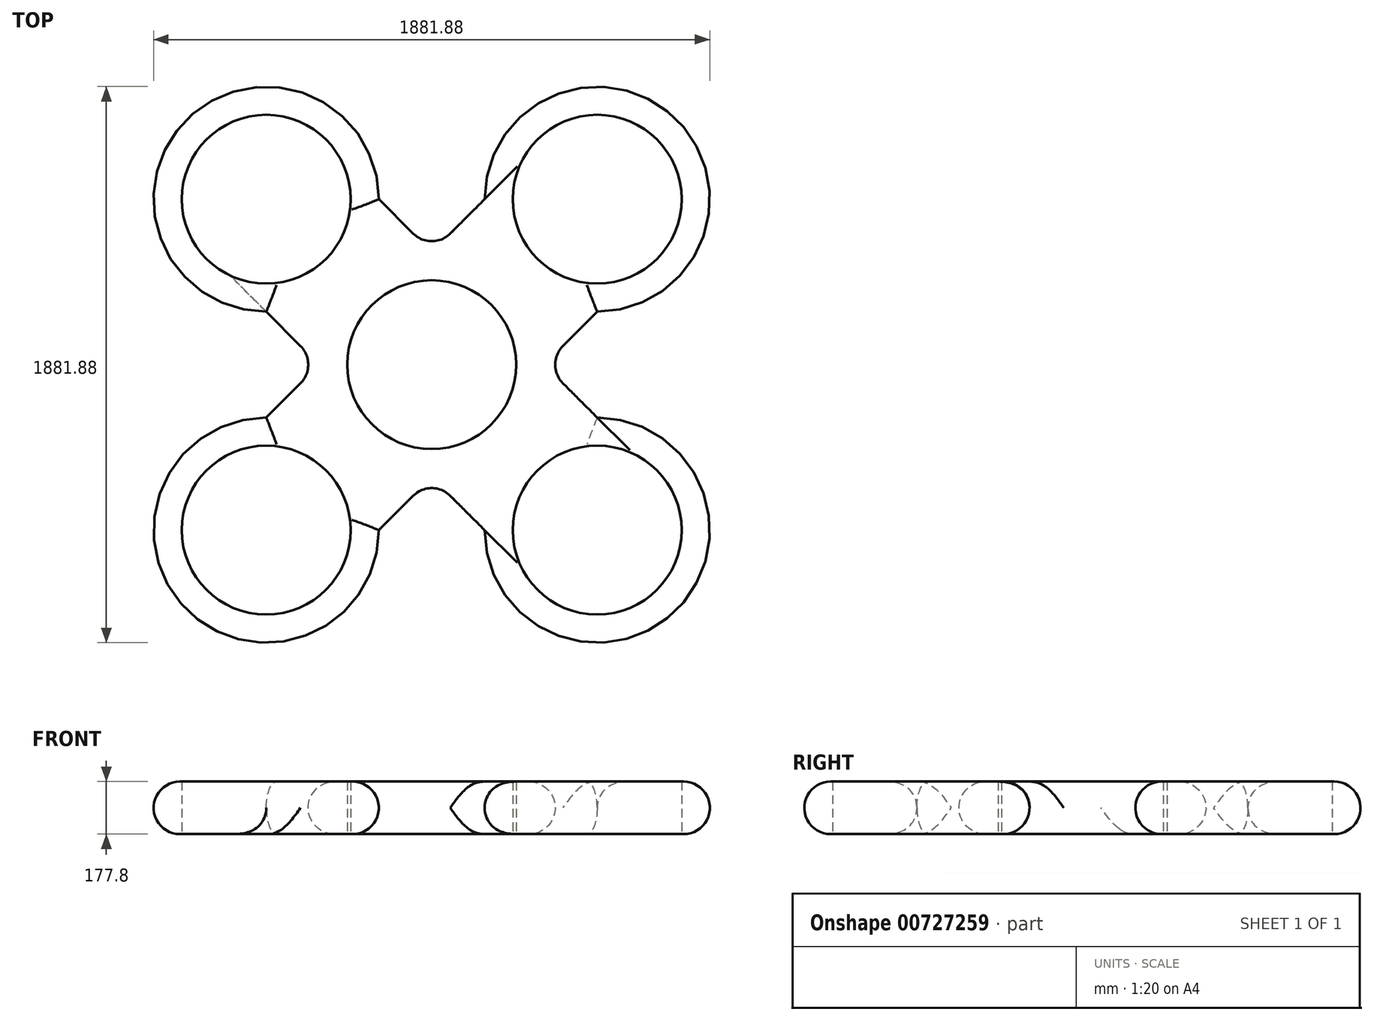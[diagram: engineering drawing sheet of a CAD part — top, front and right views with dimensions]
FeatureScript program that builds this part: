
annotation { "Feature Type Name" : "Feature", "Feature Type Description" : "" }
export const myFeature = defineFeature(function(context is Context, id is Id, definition is map)
    precondition{}
    {
        {
            var Q0;
            Q0=qCreatedBy(makeId("Top.planeOp"),FACE);
            var sketch = newSketch(context, id + "F0", { "sketchPlane" : qUnion([Q0])});
            skCircle(sketch, "E0", {"center": v(0, 0) * mm, "radius": 285.75 * mm});
            skCircle(sketch, "E1", {"center": v(0, 0) * mm, "radius": 381 * mm});
            skLineSegment(sketch, "E2", {"start": v(0, 0) * mm, "end": v(0, 762) * mm});
            skPoint(sketch, "E3.0.midPoint", {"position": v(0, 762) * mm});
            skCircle(sketch, "E4", {"center": v(-559.94, 559.94) * mm, "radius": 285.75 * mm});
            skCircle(sketch, "E5", {"center": v(-559.94, 559.94) * mm, "radius": 381 * mm});
            skLineSegment(sketch, "E6", {"start": v(0, 381) * mm, "end": v(-178.94, 559.94) * mm});
            skLineSegment(sketch, "E7", {"start": v(-381, 0) * mm, "end": v(-559.94, 178.94) * mm});
            skCircle(sketch, "E8", {"center": v(559.94, 559.94) * mm, "radius": 285.75 * mm});
            skCircle(sketch, "E9", {"center": v(559.94, 559.94) * mm, "radius": 381 * mm});
            skLineSegment(sketch, "E10", {"start": v(0, 381) * mm, "end": v(178.94, 559.94) * mm});
            skLineSegment(sketch, "E11", {"start": v(381, 0) * mm, "end": v(559.94, 178.94) * mm});
            skCircle(sketch, "E12", {"center": v(559.94, -559.94) * mm, "radius": 285.75 * mm});
            skCircle(sketch, "E13", {"center": v(559.94, -559.94) * mm, "radius": 381 * mm});
            skLineSegment(sketch, "E14", {"start": v(0, -381) * mm, "end": v(178.94, -559.94) * mm});
            skLineSegment(sketch, "E15", {"start": v(381, 0) * mm, "end": v(559.94, -178.94) * mm});
            skCircle(sketch, "E16", {"center": v(-559.94, -559.94) * mm, "radius": 285.75 * mm});
            skCircle(sketch, "E17", {"center": v(-559.94, -559.94) * mm, "radius": 381 * mm});
            skLineSegment(sketch, "E18", {"start": v(-381, 0) * mm, "end": v(-559.94, -178.94) * mm});
            skLineSegment(sketch, "E19", {"start": v(0, -381) * mm, "end": v(-178.94, -559.94) * mm});
            skSolve(sketch);
        }
        {
            var Q0;
            {var subQ0=sQuery(id+"F0.wireOp",EDGE,"sOMEycEi-MdqB-uUI0-WZba-tYQb8DUVvBA8");Q0=makeQuery(id+"F0.imprint","IMPRINT",FACE,{"disambiguationData":[TD([[makeQuery(id+"F0.imprint","IMPRINT",EDGE,{"derivedFrom":subQ0}),1.0]])]});}
            var Q1;
            {var subQ0=sQuery(id+"F0.wireOp",EDGE,"q6DWFzyf-PYHz-5VbU-MnMN-QwQLJZp00MLm");Q1=makeQuery(id+"F0.imprint","IMPRINT",FACE,{"disambiguationData":[TD([[makeQuery(id+"F0.imprint","IMPRINT",EDGE,{"derivedFrom":subQ0}),1.0]])]});}
            var Q2;
            {var subQ0=sQuery(id+"F0.wireOp",EDGE,"2G3Iw2K2-ujzs-mwtG-Kt6d-7udmvSFRi98N");Q2=makeQuery(id+"F0.imprint","IMPRINT",FACE,{"disambiguationData":[TD([[makeQuery(id+"F0.imprint","IMPRINT",EDGE,{"derivedFrom":subQ0}),-1.0]])]});}
            var Q3;
            {var subQ0=sQuery(id+"F0.wireOp",EDGE,"acN5SHeT-FAdY-YJyH-kvA1-sv4Ht1ptY0J2");Q3=makeQuery(id+"F0.imprint","IMPRINT",FACE,{"disambiguationData":[TD([[makeQuery(id+"F0.imprint","IMPRINT",EDGE,{"derivedFrom":subQ0}),-1.0]])]});}
            var Q4;
            Q4=makeQuery(id+"F0.imprint","IMPRINT",FACE,{"disambiguationData":[TD([[makeQuery(id+"F0.imprint","IMPRINT",EDGE,{"derivedFrom":sQuery(id+"F0.wireOp",EDGE,"E0")}),-1.0]])]});
            var Q5;
            {var subQ1=sQuery(id+"F0.wireOp",EDGE,"E3.1");var subQ3=sQuery(id+"F0.wireOp",EDGE,"RLFRBpkf-K19b-q8CQ-DwKp-c1LprMLDoz8B");var subQ4=makeQuery(id+"F0.imprint","INTERSECT",VERTEX,{"derivedFrom":[subQ1,subQ3]});Q5=makeQuery(id+"F0.imprint","IMPRINT",FACE,{"disambiguationData":[TD([[makeQuery(id+"F0.imprint","IMPRINT",EDGE,{"disambiguationData":[TD([[subQ4,-1.0]])],"derivedFrom":subQ3}),-1.0]])]});}
            var Q6;
            {var subQ1=sQuery(id+"F0.wireOp",EDGE,"E3.1");var subQ3=sQuery(id+"F0.wireOp",EDGE,"RLFRBpkf-K19b-q8CQ-DwKp-c1LprMLDoz8B");var subQ4=makeQuery(id+"F0.imprint","INTERSECT",VERTEX,{"derivedFrom":[subQ1,subQ3]});Q6=makeQuery(id+"F0.imprint","IMPRINT",FACE,{"disambiguationData":[TD([[makeQuery(id+"F0.imprint","IMPRINT",EDGE,{"disambiguationData":[TD([[subQ4,1.0]])],"derivedFrom":subQ3}),-1.0]])]});}
            var Q7;
            {var subQ1=sQuery(id+"F0.wireOp",EDGE,"E3.2");var subQ3=sQuery(id+"F0.wireOp",EDGE,"1lw6dge2-0ASI-JQR3-Ic2Y-iIIyL2x1a0zL");var subQ4=makeQuery(id+"F0.imprint","INTERSECT",VERTEX,{"derivedFrom":[subQ1,subQ3]});Q7=makeQuery(id+"F0.imprint","IMPRINT",FACE,{"disambiguationData":[TD([[makeQuery(id+"F0.imprint","IMPRINT",EDGE,{"disambiguationData":[TD([[subQ4,-1.0]])],"derivedFrom":subQ3}),-1.0]])]});}
            var Q8;
            {var subQ1=sQuery(id+"F0.wireOp",EDGE,"E3.2");var subQ3=sQuery(id+"F0.wireOp",EDGE,"1lw6dge2-0ASI-JQR3-Ic2Y-iIIyL2x1a0zL");var subQ4=makeQuery(id+"F0.imprint","INTERSECT",VERTEX,{"derivedFrom":[subQ1,subQ3]});Q8=makeQuery(id+"F0.imprint","IMPRINT",FACE,{"disambiguationData":[TD([[makeQuery(id+"F0.imprint","IMPRINT",EDGE,{"disambiguationData":[TD([[subQ4,1.0]])],"derivedFrom":subQ3}),-1.0]])]});}
            var Q9;
            {var subQ1=sQuery(id+"F0.wireOp",EDGE,"E3.0");var subQ3=sQuery(id+"F0.wireOp",EDGE,"pi5Sw7Lp-ZabZ-SSrr-5lA3-6I5oRJSt0pTV");var subQ4=makeQuery(id+"F0.imprint","INTERSECT",VERTEX,{"derivedFrom":[subQ1,subQ3]});Q9=makeQuery(id+"F0.imprint","IMPRINT",FACE,{"disambiguationData":[TD([[makeQuery(id+"F0.imprint","IMPRINT",EDGE,{"disambiguationData":[TD([[subQ4,-1.0]])],"derivedFrom":subQ3}),-1.0]])]});}
            var Q10;
            {var subQ1=sQuery(id+"F0.wireOp",EDGE,"E3.0");var subQ3=sQuery(id+"F0.wireOp",EDGE,"gQGFOENC-yvVc-tpmk-VgxU-U4rg5gfOjFKJ");var subQ4=makeQuery(id+"F0.imprint","INTERSECT",VERTEX,{"derivedFrom":[subQ1,subQ3]});Q10=makeQuery(id+"F0.imprint","IMPRINT",FACE,{"disambiguationData":[TD([[makeQuery(id+"F0.imprint","IMPRINT",EDGE,{"disambiguationData":[TD([[subQ4,1.0]])],"derivedFrom":subQ3}),-1.0]])]});}
            var Q11;
            {var subQ1=sQuery(id+"F0.wireOp",EDGE,"E3.0");var subQ3=sQuery(id+"F0.wireOp",EDGE,"gQGFOENC-yvVc-tpmk-VgxU-U4rg5gfOjFKJ");var subQ4=makeQuery(id+"F0.imprint","INTERSECT",VERTEX,{"derivedFrom":[subQ1,subQ3]});Q11=makeQuery(id+"F0.imprint","IMPRINT",FACE,{"disambiguationData":[TD([[makeQuery(id+"F0.imprint","IMPRINT",EDGE,{"disambiguationData":[TD([[subQ4,-1.0]])],"derivedFrom":subQ3}),-1.0]])]});}
            var Q12;
            {var subQ1=sQuery(id+"F0.wireOp",EDGE,"E3.0");var subQ3=sQuery(id+"F0.wireOp",EDGE,"pi5Sw7Lp-ZabZ-SSrr-5lA3-6I5oRJSt0pTV");var subQ4=makeQuery(id+"F0.imprint","INTERSECT",VERTEX,{"derivedFrom":[subQ1,subQ3]});Q12=makeQuery(id+"F0.imprint","IMPRINT",FACE,{"disambiguationData":[TD([[makeQuery(id+"F0.imprint","IMPRINT",EDGE,{"disambiguationData":[TD([[subQ4,1.0]])],"derivedFrom":subQ3}),-1.0]])]});}
            extrude(context, id + "F1", {"entities" : qUnion([Q0, Q1, Q2, Q3, Q4, Q5, Q6, Q7, Q8, Q9, Q10, Q11, Q12]), "depth" : 177.8 * mm, "offsetDistance" : 25.4 * mm});
        }
        {
            var Q0;
            Q0 = qSketchRegion(id + "F0", true);
            extrude(context, id + "F2", {"entities" : qUnion([Q0]), "operationType" : NewBodyOperationType.ADD, "depth" : 177.8 * mm, "offsetDistance" : 25.4 * mm});
        }
        {
            var Q0;
            Q0=makeQuery(id+"F2.opExtrude","CAP_EDGE",EDGE,{"disambiguationData":[OSD([sQuery(id+"F0.wireOp",EDGE,"E17")])],"isStart":false});
            var Q1;
            Q1=makeQuery(id+"F2.opExtrude","CAP_EDGE",EDGE,{"disambiguationData":[OSD([sQuery(id+"F0.wireOp",EDGE,"E17")])],"isStart":true});
            var Q2;
            Q2=makeQuery(id+"F2.opExtrude","CAP_EDGE",EDGE,{"disambiguationData":[OSD([sQuery(id+"F0.wireOp",EDGE,"E19")])],"isStart":false});
            var Q3;
            Q3=makeQuery(id+"F2.opExtrude","CAP_EDGE",EDGE,{"disambiguationData":[OSD([sQuery(id+"F0.wireOp",EDGE,"E19")])],"isStart":true});
            var Q4;
            Q4=makeQuery(id+"F2.opExtrude","SWEPT_EDGE",EDGE,{"disambiguationData":[OSD([sQuery(id+"F0.wireOp",EDGE,"E1"),sQuery(id+"F0.wireOp",EDGE,"E14"),sQuery(id+"F0.wireOp",EDGE,"E19")])]});
            var Q5;
            Q5=makeQuery(id+"F2.opExtrude","SWEPT_EDGE",EDGE,{"disambiguationData":[OSD([sQuery(id+"F0.wireOp",EDGE,"E1"),sQuery(id+"F0.wireOp",EDGE,"E7"),sQuery(id+"F0.wireOp",EDGE,"E18")])]});
            var Q6;
            Q6=makeQuery(id+"F2.opExtrude","CAP_EDGE",EDGE,{"disambiguationData":[OSD([sQuery(id+"F0.wireOp",EDGE,"E5")])],"isStart":false});
            var Q7;
            Q7=makeQuery(id+"F2.opExtrude","CAP_EDGE",EDGE,{"disambiguationData":[OSD([sQuery(id+"F0.wireOp",EDGE,"E5")])],"isStart":true});
            var Q8;
            Q8=makeQuery(id+"F2.opExtrude","CAP_EDGE",EDGE,{"disambiguationData":[OSD([sQuery(id+"F0.wireOp",EDGE,"E18")])],"isStart":false});
            var Q9;
            Q9=makeQuery(id+"F2.opExtrude","CAP_EDGE",EDGE,{"disambiguationData":[OSD([sQuery(id+"F0.wireOp",EDGE,"E7")])],"isStart":false});
            var Q10;
            Q10=makeQuery(id+"F2.opExtrude","SWEPT_EDGE",EDGE,{"disambiguationData":[OSD([sQuery(id+"F0.wireOp",EDGE,"E1"),sQuery(id+"F0.wireOp",EDGE,"E6"),sQuery(id+"F0.wireOp",EDGE,"E10")])]});
            var Q11;
            Q11=makeQuery(id+"F2.opExtrude","CAP_EDGE",EDGE,{"disambiguationData":[OSD([sQuery(id+"F0.wireOp",EDGE,"E6")])],"isStart":false});
            var Q12;
            Q12=makeQuery(id+"F2.opExtrude","CAP_EDGE",EDGE,{"disambiguationData":[OSD([sQuery(id+"F0.wireOp",EDGE,"E6")])],"isStart":true});
            var Q13;
            Q13=makeQuery(id+"F2.opExtrude","CAP_EDGE",EDGE,{"disambiguationData":[OSD([sQuery(id+"F0.wireOp",EDGE,"E9")])],"isStart":true});
            var Q14;
            Q14=makeQuery(id+"F2.opExtrude","CAP_EDGE",EDGE,{"disambiguationData":[OSD([sQuery(id+"F0.wireOp",EDGE,"E9")])],"isStart":false});
            var Q15;
            Q15=makeQuery(id+"F2.opExtrude","SWEPT_EDGE",EDGE,{"disambiguationData":[OSD([sQuery(id+"F0.wireOp",EDGE,"E1"),sQuery(id+"F0.wireOp",EDGE,"E11"),sQuery(id+"F0.wireOp",EDGE,"E15")])]});
            var Q16;
            Q16=makeQuery(id+"F2.opExtrude","CAP_EDGE",EDGE,{"disambiguationData":[OSD([sQuery(id+"F0.wireOp",EDGE,"E11")])],"isStart":true});
            var Q17;
            Q17=makeQuery(id+"F2.opExtrude","CAP_EDGE",EDGE,{"disambiguationData":[OSD([sQuery(id+"F0.wireOp",EDGE,"E15")])],"isStart":true});
            var Q18;
            Q18=makeQuery(id+"F2.opExtrude","CAP_EDGE",EDGE,{"disambiguationData":[OSD([sQuery(id+"F0.wireOp",EDGE,"E13")])],"isStart":true});
            var Q19;
            Q19=makeQuery(id+"F2.opExtrude","CAP_EDGE",EDGE,{"disambiguationData":[OSD([sQuery(id+"F0.wireOp",EDGE,"E13")])],"isStart":false});
            var Q20;
            Q20=makeQuery(id+"F2.opExtrude","CAP_EDGE",EDGE,{"disambiguationData":[OSD([sQuery(id+"F0.wireOp",EDGE,"E11")])],"isStart":false});
            var Q21;
            Q21=makeQuery(id+"F2.opExtrude","CAP_EDGE",EDGE,{"disambiguationData":[OSD([sQuery(id+"F0.wireOp",EDGE,"E18")])],"isStart":true});
            fillet(context, id + "F3", {"entities" : qUnion([Q0, Q1, Q2, Q3, Q4, Q5, Q6, Q7, Q8, Q9, Q10, Q11, Q12, Q13, Q14, Q15, Q16, Q17, Q18, Q19, Q20, Q21]), "radius" : 88.9 * mm, "tangentPropagation" : true, "allowEdgeOverflow" : false});
        }
    });
